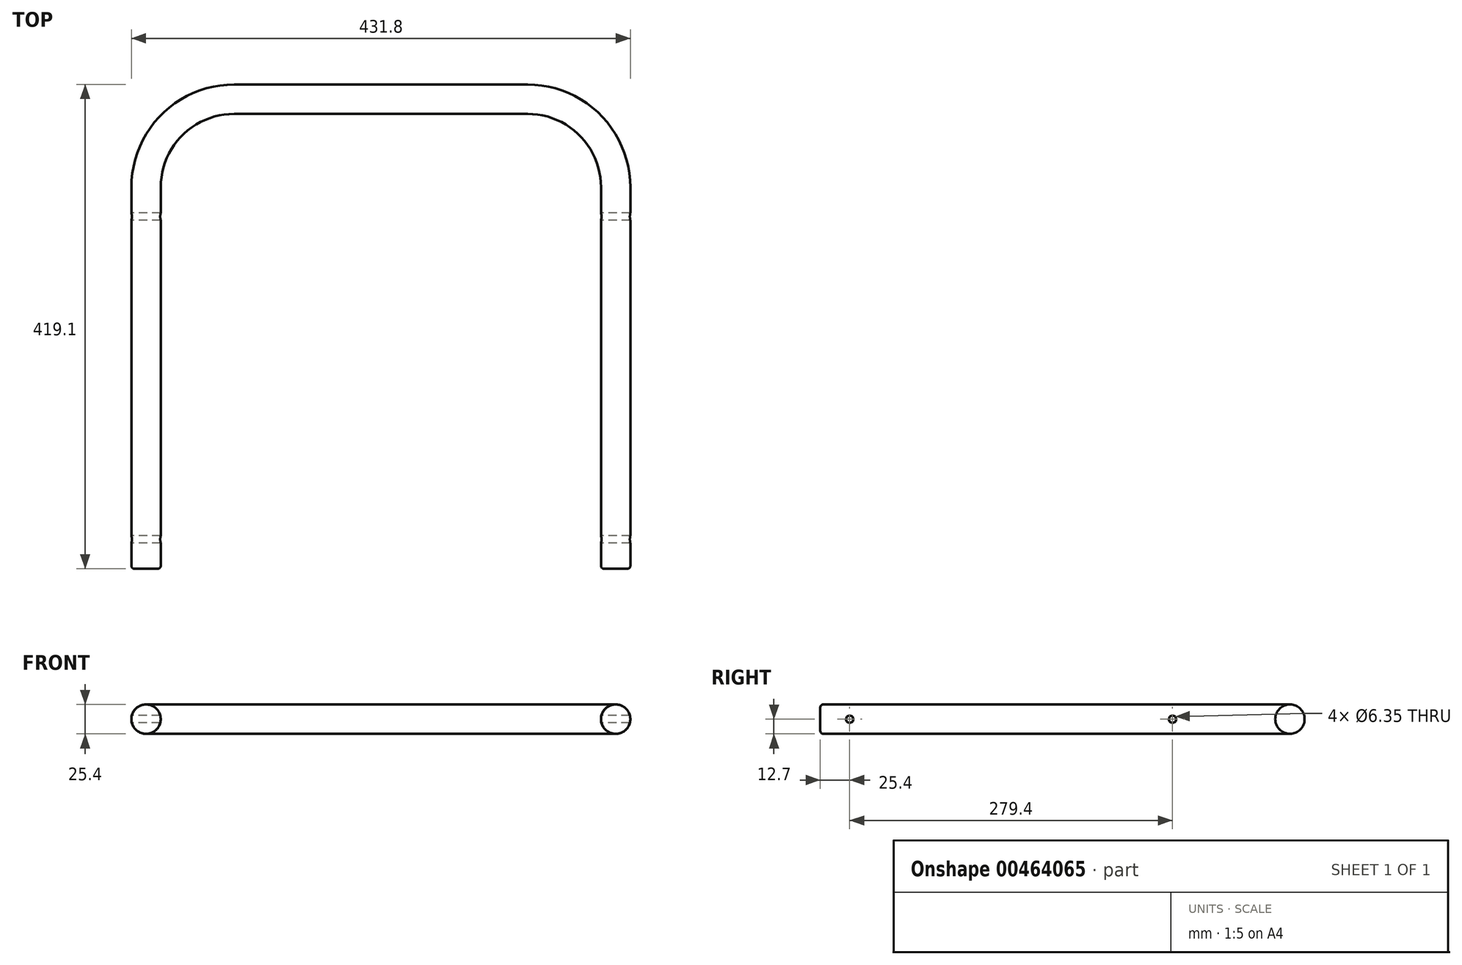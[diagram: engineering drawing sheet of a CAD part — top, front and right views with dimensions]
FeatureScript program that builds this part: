
annotation { "Feature Type Name" : "Feature", "Feature Type Description" : "" }
export const myFeature = defineFeature(function(context is Context, id is Id, definition is map)
    precondition{}
    {
        {
            var Q0;
            Q0=qCreatedBy(makeId("Front.planeOp"),FACE);
            cPlane(context, id + "F0", {"entities" : qUnion([Q0]), "cplaneType" : CPlaneType.OFFSET, "offset" : 101.6 * mm, "width" : 152.4 * mm, "height" : 152.4 * mm});
        }
        {
            var Q0;
            Q0=qCreatedBy(makeId("Top.planeOp"),FACE);
            var sketch = newSketch(context, id + "F1", { "sketchPlane" : qUnion([Q0])});
            skLineSegment(sketch, "E0", {"start": v(0, 0) * mm, "end": v(-203.2, 0) * mm});
            skLineSegment(sketch, "E1", {"start": v(-203.2, 0) * mm, "end": v(-203.2, 228.6) * mm});
            skLineSegment(sketch, "E2", {"start": v(0, 0) * mm, "end": v(0, 304.8) * mm});
            skLineSegment(sketch, "E3", {"start": v(0, 304.8) * mm, "end": v(-127, 304.8) * mm});
            skArc(sketch, "E4", {"start": v(-127, 304.8) * mm, "mid": v(-180.88, 282.48) * mm, "end": v(-203.2, 228.6) * mm});
            skLineSegment(sketch, "E5.MirrorCS", {"start": v(0, 304.8) * mm, "end": v(127, 304.8) * mm});
            skArc(sketch, "E6.MirrorCS", {"start": v(127, 304.8) * mm, "mid": v(180.88, 282.48) * mm, "end": v(203.2, 228.6) * mm});
            skLineSegment(sketch, "E7.MirrorCS", {"start": v(203.2, 0) * mm, "end": v(203.2, 228.6) * mm});
            skLineSegment(sketch, "E8", {"start": v(-203.2, 0) * mm, "end": v(-203.2, -101.6) * mm});
            skSolve(sketch);
        }
        {
            var Q0;
            Q0=qCreatedBy(id+"F0.planeOp",FACE);
            var sketch = newSketch(context, id + "F2", { "sketchPlane" : qUnion([Q0])});
            skLineSegment(sketch, "E9", {"start": v(0, 0) * mm, "end": v(-203.2, 0) * mm});
            skCircle(sketch, "E10", {"center": v(-203.2, 0) * mm, "radius": 12.7 * mm});
            skSolve(sketch);
        }
        {
            var Q0;
            Q0=makeQuery(id+"F2.imprint","IMPRINT",FACE,{"disambiguationData":[TD([[makeQuery(id+"F2.imprint","IMPRINT",EDGE,{"derivedFrom":sQuery(id+"F2.wireOp",EDGE,"E10")}),1.0]])]});
            var Q1;
            Q1=sQuery(id+"F1.wireOp",EDGE,"E5.MirrorCS");
            var Q2;
            Q2=sQuery(id+"F1.wireOp",EDGE,"E6.MirrorCS");
            var Q3;
            Q3=sQuery(id+"F1.wireOp",EDGE,"E3");
            var Q4;
            Q4=sQuery(id+"F1.wireOp",EDGE,"E1");
            var Q5;
            Q5=sQuery(id+"F1.wireOp",EDGE,"E7.MirrorCS");
            var Q6;
            Q6=sQuery(id+"F1.wireOp",EDGE,"E4");
            var Q7;
            Q7=sQuery(id+"F1.wireOp",EDGE,"E8");
            sweep(context, id + "F3", {"profiles" : qUnion([Q0]), "path" : qUnion([Q1, Q2, Q3, Q4, Q5, Q6, Q7])});
        }
        {
            var Q0;
            Q0=qCreatedBy(makeId("Right.planeOp"),FACE);
            cPlane(context, id + "F4", {"entities" : qUnion([Q0]), "cplaneType" : CPlaneType.OFFSET, "offset" : 203.2 * mm, "width" : 152.4 * mm, "height" : 152.4 * mm});
        }
        {
            var Q0;
            Q0=qCreatedBy(id+"F4.planeOp",FACE);
            var sketch = newSketch(context, id + "F5", { "sketchPlane" : qUnion([Q0])});
            skLineSegment(sketch, "E11", {"start": v(0, 0) * mm, "end": v(203.2, 0) * mm});
            skCircle(sketch, "E12", {"center": v(203.2, 0) * mm, "radius": 3.18 * mm});
            skSolve(sketch);
        }
        {
            var Q0;
            Q0 = qSketchRegion(id + "F5", true);
            extrude(context, id + "F6", {"entities" : qUnion([Q0]), "operationType" : NewBodyOperationType.REMOVE, "depth" : 19.05 * mm, "hasSecondDirection" : true, "secondDirectionOppositeDirection" : true, "secondDirectionDepth" : 430.53 * mm});
        }
        {
            var Q0;
            Q0=makeQuery(id+"F3.opSweep","SWEPT_BODY",BODY,{"disambiguationData":[OSD([sQuery(id+"F1.wireOp",EDGE,"E1"),sQuery(id+"F2.wireOp",EDGE,"E10")])]});
            var Q1;
            Q1=qCreatedBy(makeId("Right.planeOp"),FACE);
            mirror(context, id + "F7", {"operationType" : NewBodyOperationType.ADD, "entities" : qUnion([Q0]), "mirrorPlane" : qUnion([Q1])});
        }
        {
            var Q0;
            Q0=qCreatedBy(id+"F4.planeOp",FACE);
            var sketch = newSketch(context, id + "F8", { "sketchPlane" : qUnion([Q0])});
            skLineSegment(sketch, "E13", {"start": v(0, 0) * mm, "end": v(-76.2, 0) * mm});
            skCircle(sketch, "E14", {"center": v(-76.2, 0) * mm, "radius": 3.18 * mm});
            skSolve(sketch);
        }
        {
            var Q0;
            Q0 = qSketchRegion(id + "F8", true);
            extrude(context, id + "F9", {"entities" : qUnion([Q0]), "operationType" : NewBodyOperationType.REMOVE, "depth" : 19.05 * mm, "hasSecondDirection" : true, "secondDirectionOppositeDirection" : true, "secondDirectionDepth" : 425.96 * mm});
        }
        {
            var Q0;
            Q0=makeQuery(id+"F3.opSweep","CAP_EDGE",EDGE,{"disambiguationData":[OSD([sQuery(id+"F1.wireOp",VERTEX,"E8.end"),sQuery(id+"F2.wireOp",EDGE,"E10")])],"isStart":true});
            var Q1;
            Q1=makeQuery(id+"F7.opPattern","COPY",EDGE,{"derivedFrom":makeQuery(id+"F3.opSweep","CAP_EDGE",EDGE,{"disambiguationData":[OSD([sQuery(id+"F1.wireOp",VERTEX,"E8.end"),sQuery(id+"F2.wireOp",EDGE,"E10")])],"isStart":true}),"instanceName":"1"});
            fillet(context, id + "F10", {"entities" : qUnion([Q0, Q1]), "radius" : 2.54 * mm, "tangentPropagation" : true, "allowEdgeOverflow" : false});
        }
    });
